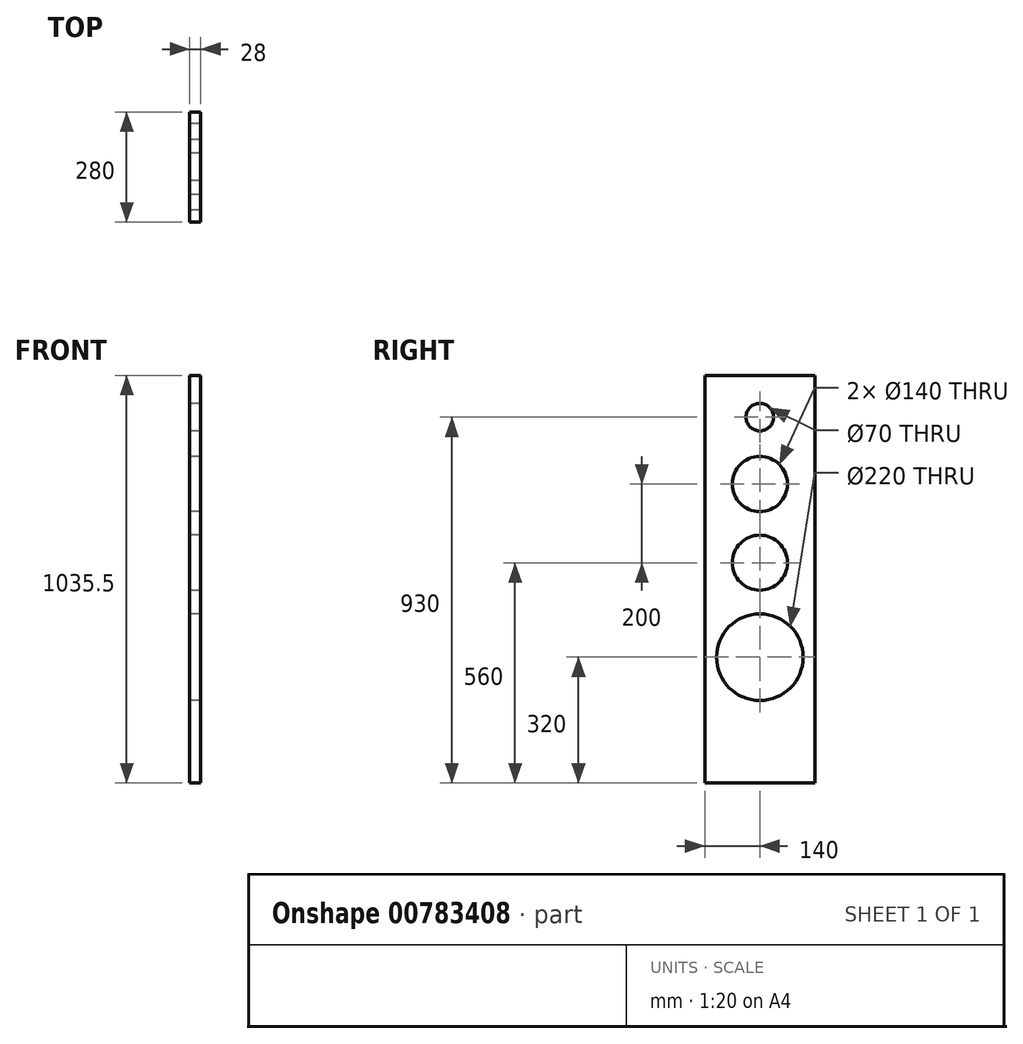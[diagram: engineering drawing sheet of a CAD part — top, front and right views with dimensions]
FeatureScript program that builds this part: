
annotation { "Feature Type Name" : "Feature", "Feature Type Description" : "" }
export const myFeature = defineFeature(function(context is Context, id is Id, definition is map)
    precondition{}
    {
        {
            var Q0;
            Q0=qCreatedBy(makeId("Top.planeOp"),FACE);
            var sketch = newSketch(context, id + "F0", { "sketchPlane" : qUnion([Q0])});
            skLineSegment(sketch, "E0", {"start": v(-14, 140) * mm, "end": v(-14, -140) * mm});
            skLineSegment(sketch, "E1.0", {"start": v(14, 140) * mm, "end": v(14, -140) * mm});
            skLineSegment(sketch, "E2", {"start": v(-14, -140) * mm, "end": v(14, -140) * mm});
            skLineSegment(sketch, "E3", {"start": v(-14, 140) * mm, "end": v(14, 140) * mm});
            skSolve(sketch);
        }
        {
            var Q0;
            Q0=makeQuery(id+"F0.imprint","IMPRINT",FACE,{"disambiguationData":[TD([[makeQuery(id+"F0.imprint","IMPRINT",EDGE,{"derivedFrom":sQuery(id+"F0.wireOp",EDGE,"E0")}),1.0]])]});
            extrude(context, id + "F1", {"entities" : qUnion([Q0]), "depth" : 1035.5 * mm, "offsetDistance" : 25 * mm});
        }
        {
            var Q0;
            Q0=qCreatedBy(makeId("Right.planeOp"),FACE);
            var sketch = newSketch(context, id + "F2", { "sketchPlane" : qUnion([Q0])});
            skLineSegment(sketch, "E4", {"start": v(0, 1301.74) * mm, "end": v(0, -385.83) * mm, "construction": true});
            skCircle(sketch, "E5", {"center": v(0, 320) * mm, "radius": 110 * mm});
            skCircle(sketch, "E6", {"center": v(0, 560) * mm, "radius": 70 * mm});
            skCircle(sketch, "E7", {"center": v(0, 760) * mm, "radius": 70 * mm});
            skCircle(sketch, "E8", {"center": v(0, 930) * mm, "radius": 35 * mm});
            skSolve(sketch);
        }
        {
            var Q0;
            Q0 = qSketchRegion(id + "F2", true);
            extrude(context, id + "F3", {"entities" : qUnion([Q0]), "operationType" : NewBodyOperationType.REMOVE, "endBound" : BoundingType.SYMMETRIC, "depth" : 100 * mm, "offsetDistance" : 25 * mm});
        }
    });
